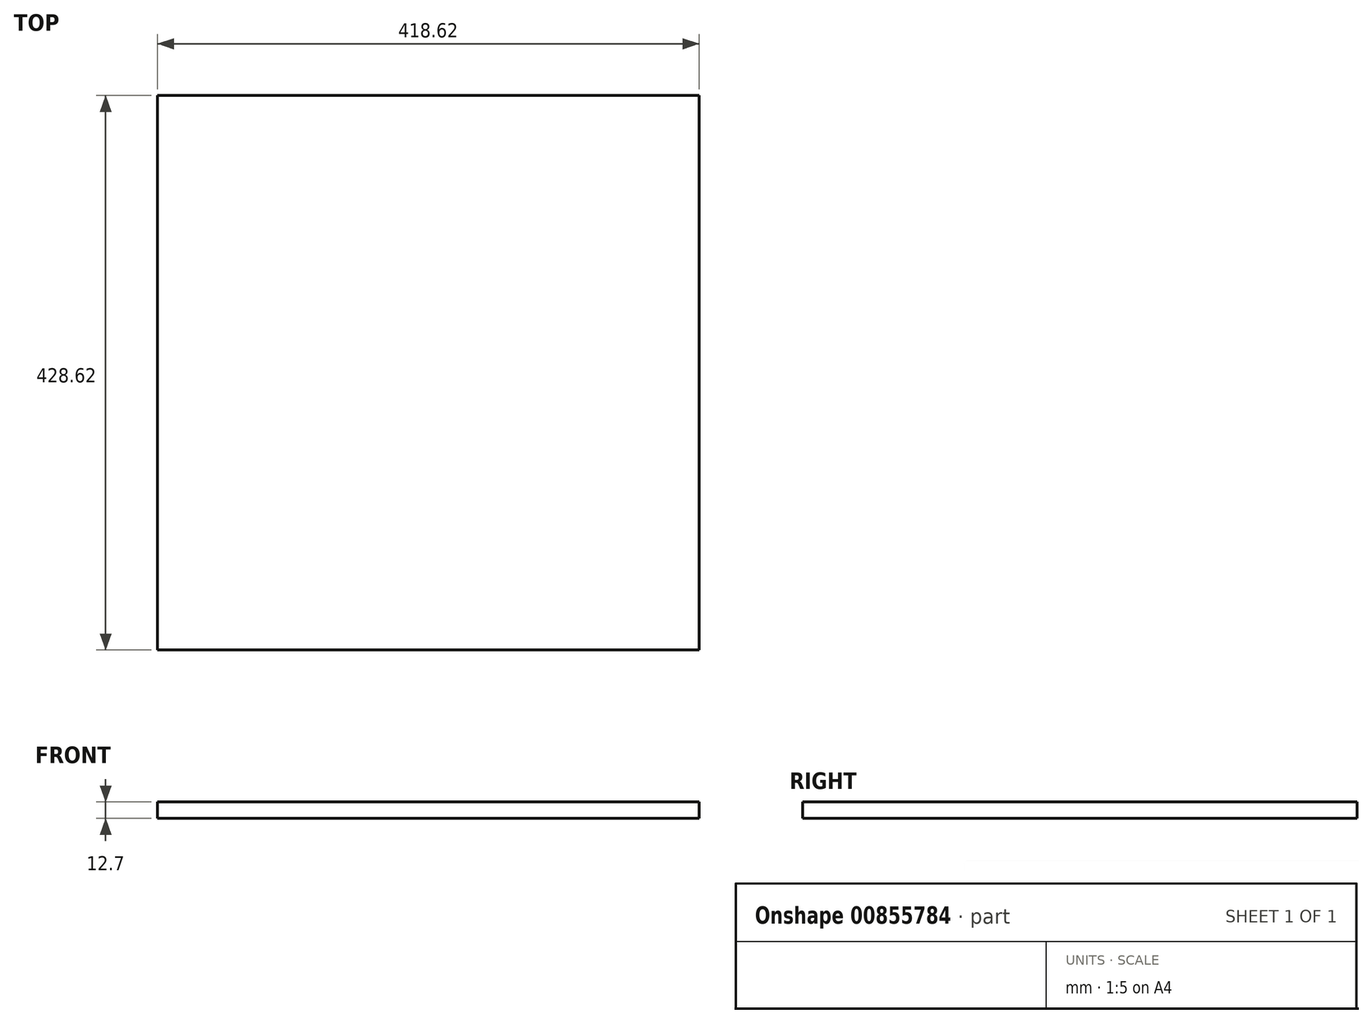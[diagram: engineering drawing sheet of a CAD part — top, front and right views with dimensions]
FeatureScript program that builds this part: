
annotation { "Feature Type Name" : "Feature", "Feature Type Description" : "" }
export const myFeature = defineFeature(function(context is Context, id is Id, definition is map)
    precondition{}
    {
        {
            var Q0;
            Q0=qCreatedBy(makeId("Top.planeOp"),FACE);
            var sketch = newSketch(context, id + "F0", { "sketchPlane" : qUnion([Q0])});
            skLineSegment(sketch, "E0.bottom", {"start": v(209.31, -214.31) * mm, "end": v(-209.31, -214.31) * mm});
            skLineSegment(sketch, "E0.top", {"start": v(209.31, 214.31) * mm, "end": v(-209.31, 214.31) * mm});
            skLineSegment(sketch, "E0.left", {"start": v(209.31, -214.31) * mm, "end": v(209.31, 214.31) * mm});
            skLineSegment(sketch, "E0.right", {"start": v(-209.31, -214.31) * mm, "end": v(-209.31, 214.31) * mm});
            skPoint(sketch, "E0.middle", {"position": v(0, 0) * mm});
            skSolve(sketch);
        }
        {
            var Q0;
            Q0=makeQuery(id+"F0.imprint","IMPRINT",FACE,{"disambiguationData":[TD([[makeQuery(id+"F0.imprint","IMPRINT",EDGE,{"derivedFrom":sQuery(id+"F0.wireOp",EDGE,"E0.bottom")}),-1.0]])]});
            extrude(context, id + "F1", {"entities" : qUnion([Q0]), "oppositeDirection" : true, "depth" : 12.7 * mm, "offsetDistance" : 25.4 * mm});
        }
    });
